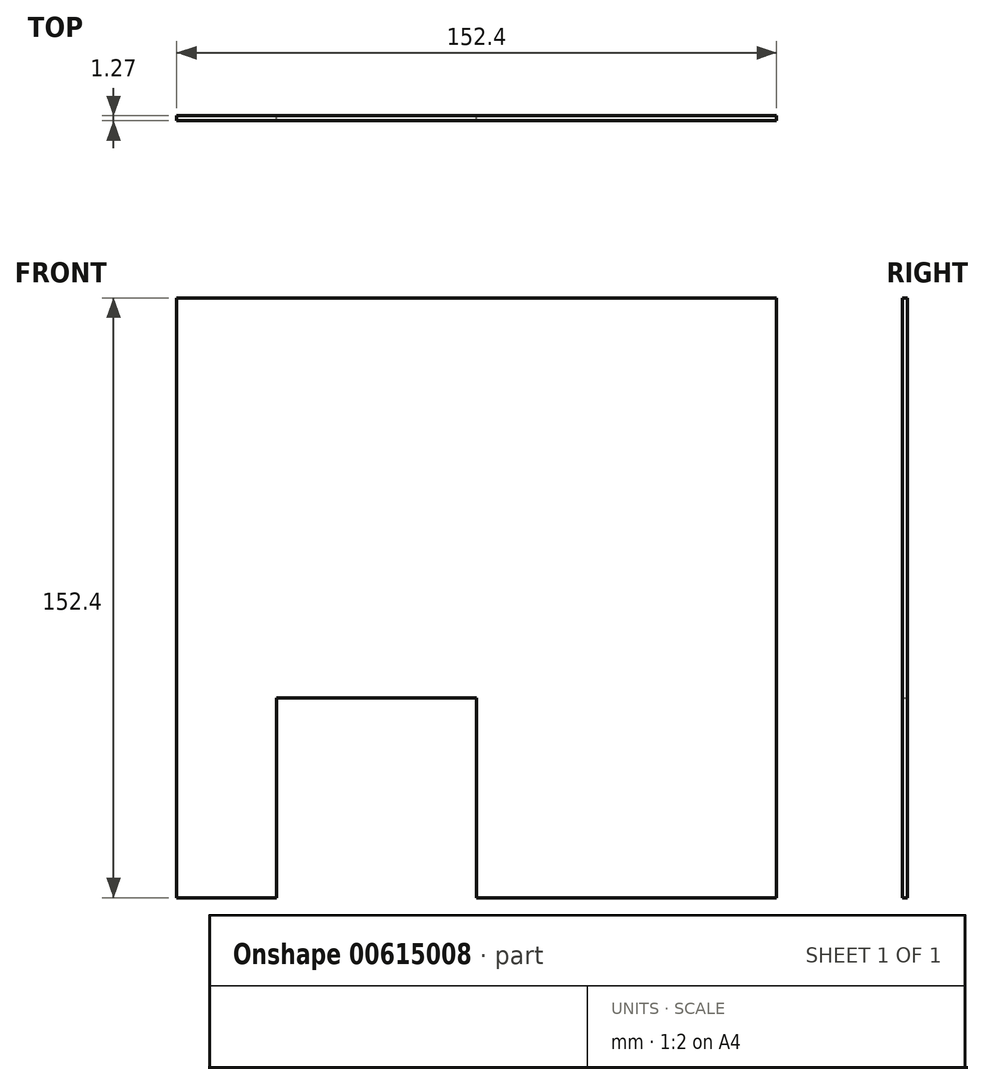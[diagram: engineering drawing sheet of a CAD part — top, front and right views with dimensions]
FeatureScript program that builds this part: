
annotation { "Feature Type Name" : "Feature", "Feature Type Description" : "" }
export const myFeature = defineFeature(function(context is Context, id is Id, definition is map)
    precondition{}
    {
        {
            var Q0;
            Q0=qCreatedBy(makeId("Front.planeOp"),FACE);
            var sketch = newSketch(context, id + "F0", { "sketchPlane" : qUnion([Q0])});
            skLineSegment(sketch, "E0.top", {"start": v(76.2, 76.2) * mm, "end": v(-76.2, 76.2) * mm});
            skLineSegment(sketch, "E0.left", {"start": v(76.2, -76.2) * mm, "end": v(76.2, 76.2) * mm});
            skLineSegment(sketch, "E0.right", {"start": v(-76.2, -76.2) * mm, "end": v(-76.2, 76.2) * mm});
            skPoint(sketch, "E0.middle", {"position": v(0, 0) * mm});
            skLineSegment(sketch, "E1", {"start": v(-76.2, -76.2) * mm, "end": v(-50.8, -76.2) * mm});
            skLineSegment(sketch, "E2", {"start": v(0, -76.2) * mm, "end": v(76.2, -76.2) * mm});
            skLineSegment(sketch, "E3", {"start": v(-50.8, -76.2) * mm, "end": v(-50.8, -25.4) * mm});
            skLineSegment(sketch, "E4", {"start": v(-50.8, -25.4) * mm, "end": v(0, -25.4) * mm});
            skLineSegment(sketch, "E5", {"start": v(0, -25.4) * mm, "end": v(0, -76.2) * mm});
            skSolve(sketch);
        }
        {
            var Q0;
            Q0 = qSketchRegion(id + "F0", true);
            extrude(context, id + "F1", {"entities" : qUnion([Q0]), "depth" : 1.27 * mm, "offsetDistance" : 25.4 * mm});
        }
    });
